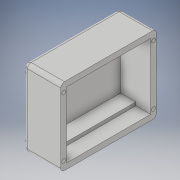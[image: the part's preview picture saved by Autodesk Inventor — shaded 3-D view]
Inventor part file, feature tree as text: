
AUTODESK INVENTOR PART (.ipt)
format: ipt  version: 2017 (Build 210142000, 142)  size: 172,032 bytes
history: native  units: in
note: dims shown in document units (in); Inventor stores cm internally (conversion verified against a paired STEP export)
features: extrude x4, sketch x4, fillet x2
ambient origin geometry x8: Origin, YZ Plane, XZ Plane, XY Plane, X Axis, Y Axis, Z Axis, Center Point
bodies: Solid1 (feature_tree)
feature tree (10):
  extrude  "Extrusion1"  Depth=3.225in
  fillet  "Fillet1"  Radius=1.25in
  extrude  "Extrusion2"  Depth=2.225in
  extrude  "Extrusion3"  Depth=0.5in TaperAngle=0.0deg
  fillet  "Fillet3"  Radius=0.1875in
  extrude  "Extrusion4"  Depth=2.85in
  sketch  "Sketch1"  dims[d0=2.6in d1=3.225in d2=1.25in d3=0.0in]
  sketch  "Sketch2"  dims[d4=0.125in d6=2.225in]
  sketch  "Sketch3"  dims[d7=2.85in d8=0.5in d9=0.0in d10=0.1875in]
  sketch  "Sketch4"  dims[d11=2.0in d12=2.85in d13=0.52in d14=0.0in d17=0.0938in d18=0.1285in d19=0.1875in d20=0.125in d21=1.0in d22=1.25in d23=0.0in]
